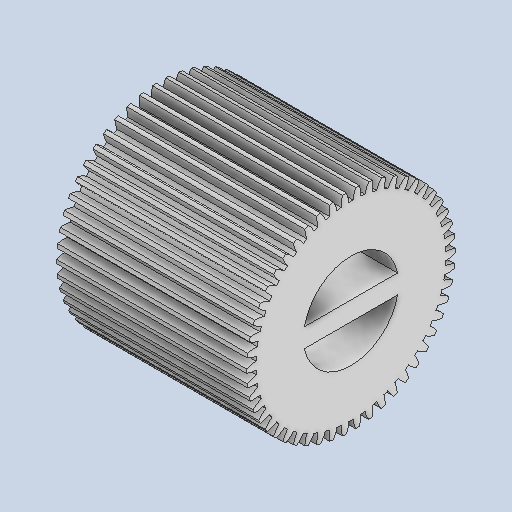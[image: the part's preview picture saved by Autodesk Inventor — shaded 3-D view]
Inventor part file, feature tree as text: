
AUTODESK INVENTOR PART (.ipt)
format: ipt  version: 2024 (Build 280153000, 153)  size: 636,928 bytes
history: native  units: mm
features: extrude x3, sketch x3, other x1
ambient origin geometry x8: Origin, YZ Plane, XZ Plane, XY Plane, X Axis, Y Axis, Z Axis, Center Point
bodies: Body1 (feature_tree)
feature tree (7):
  other  "솔리드1"
  extrude  "돌출1"  Depth=500.0mm TaperAngle=360.0deg
  extrude  "돌출2"  Depth=10.0mm TaperAngle=0.0deg
  extrude  "돌출3"  Depth=5.0mm
  sketch  "스케치1"
  sketch  "스케치2"
  sketch  "스케치3"
